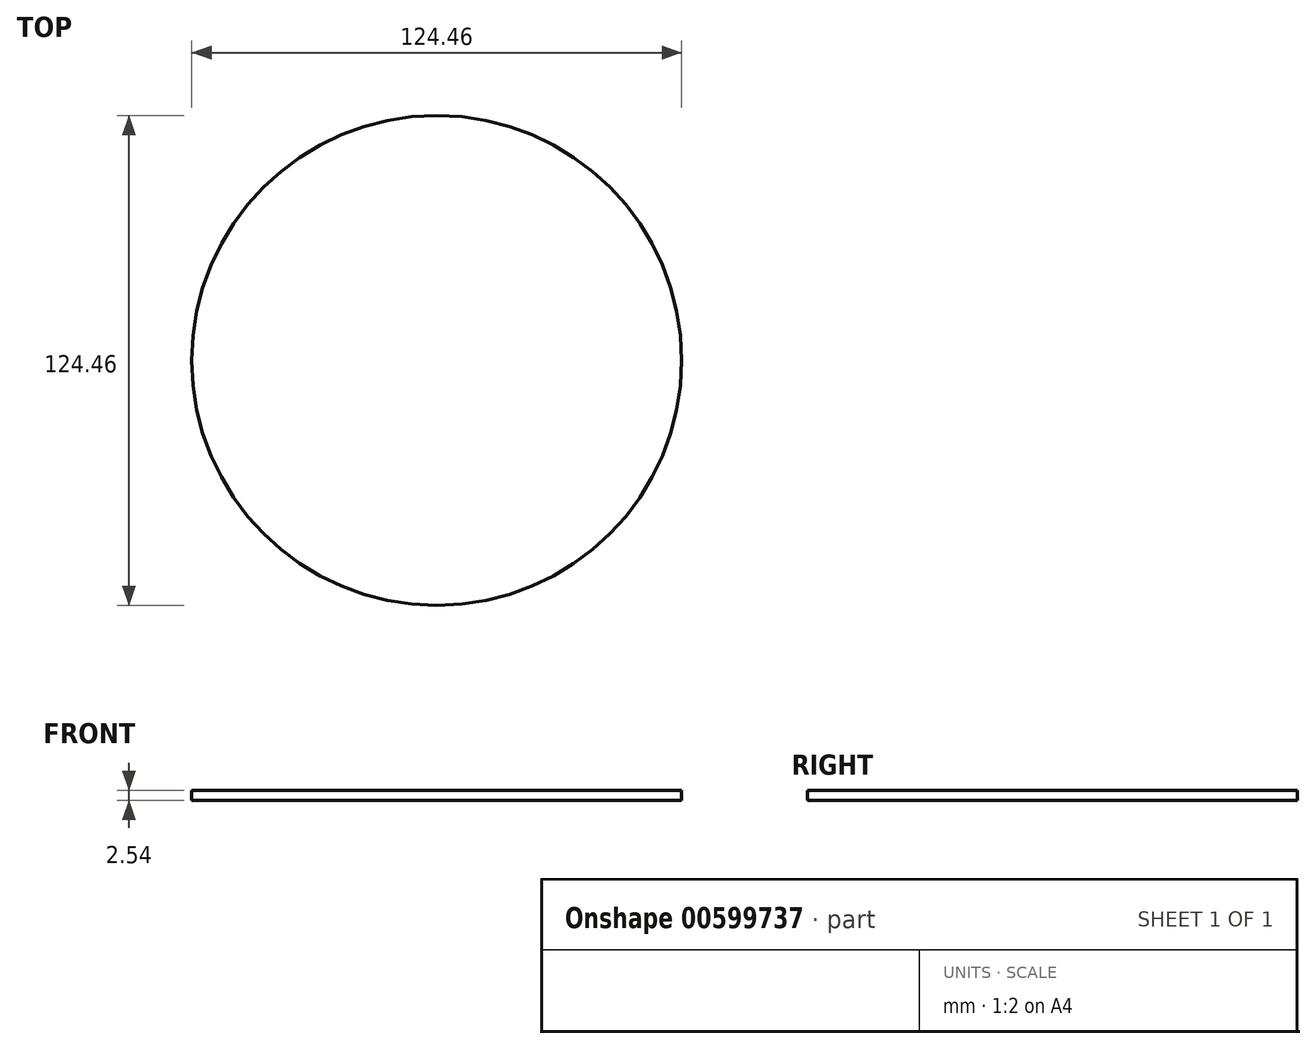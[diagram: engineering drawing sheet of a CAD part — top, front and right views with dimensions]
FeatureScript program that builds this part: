
annotation { "Feature Type Name" : "Feature", "Feature Type Description" : "" }
export const myFeature = defineFeature(function(context is Context, id is Id, definition is map)
    precondition{}
    {
        {
            var Q0;
            Q0=qCreatedBy(makeId("Top.planeOp"),FACE);
            var sketch = newSketch(context, id + "F0", { "sketchPlane" : qUnion([Q0])});
            skCircle(sketch, "E0", {"center": v(0, 0) * mm, "radius": 62.23 * mm});
            skSolve(sketch);
        }
        {
            var Q0;
            Q0 = qSketchRegion(id + "F0", true);
            extrude(context, id + "F1", {"entities" : qUnion([Q0]), "depth" : 2.54 * mm, "offsetDistance" : 25.4 * mm});
        }
    });
